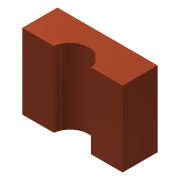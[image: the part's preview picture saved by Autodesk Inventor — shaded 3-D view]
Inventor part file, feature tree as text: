
AUTODESK INVENTOR PART (.ipt)
format: ipt  version: 2016 SP2 (Build 200236200, 236)  size: 126,464 bytes
history: native  units: mm
features: sketch x3, hole x2, extrude x1
ambient origin geometry x8: Origin, YZ Plane, XZ Plane, XY Plane, X Axis, Y Axis, Z Axis, Center Point
bodies: Body1 (feature_tree)
feature tree (6):
  extrude  "Extrusion3"  Depth=14.0mm
  sketch  "Sketch2"  dims[d6=15.0mm d7=1.0mm]
  hole  "Hole2"  [1 undecoded]
  sketch  "Sketch1"  dims[d4=40.0mm d5=14.0mm]
  sketch  "Sketch3"  dims[d8=1.0mm d9=30.0mm d10=0.0mm d11=15.0mm d12=25.0mm d13=15.0mm d14=5.5mm d15=6.0mm d16=10.0mm d17=5.7mm d18=90.0deg d19=8.0mm d20=0.0mm]
  hole  "Hole1"  [1 undecoded]
note: 2 required parameter values undecoded (feature->parameter linkage not recoverable at this tier; creation-order binding heuristic only, values carry confidence <= 0.55)
